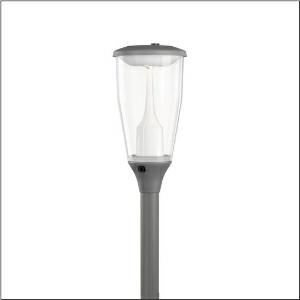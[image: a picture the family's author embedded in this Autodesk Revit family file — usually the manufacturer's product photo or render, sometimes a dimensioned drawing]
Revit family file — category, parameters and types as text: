
# Revit family: dl_11_iq___st1_2a_5xa5565ew14hp00022_746d
name_source: partatom
category: Lighting Fixtures
units: mm (PartAtom-declared; Revit-internal decimal feet)

## family parameters
Cut with Voids When Loaded = No
Host = Face
Light Source = No
Part Type = Normal
Room Calculation Point = No
Round Connector Dimension = Use Diameter
Shared = No

## types (1)
- --- (1 x LED, 4790 lm, 33.5 W, 3000K)
    Apparent Load = 34 VA
    CIE Flux Codes = 23 60 93 95 100
    Color Rendering = 70
    Color Temperature = 3000K
    Default Elevation = 1800 mm
    Description = DL 11 iQ, mast luminaire, Module 540 iQ-SR, primary light control with 3 zone facetted reflector, of plastic, silver coated, highly specular, structured, primary optical cover: cover, of PMMA, transparent, light distribution: ST1.2a, light emission: direct distribution, primary light characteristic: asymmetric, installation type: post-top, LED, High Power LED, rated luminous flux: 4.790lm, luminous efficacy: 143lm/W, light colour: 730, colour temperature: 3000K, control gear: iQ-Street Remote, D4i with power reduction, control: pre-setting: logarithmic dimming characteristic, Street-Remote, Auto-Match, Temp-Guard, Lumen-Switch, Night-Set, Smart-Wire, Light-Fading, Desk-Remote (wireless, voltage-free reading and setting of iQ features in the workshop via application-optimized NFC function/RFID function), optimised constant luminous flux control (CLO 2.0), mains connection: 220..240V, AC, 50/60Hz, connection cable pre-assembled, cable length: 5,5m, start of lifetime: 34W, end of service life: 36W, reduction: 15W, luminaire housing, upper part, of diecast aluminium, coated, Siteco® metallic grey (DB 702S), spigot size: 60mm (post-top), mounting height: 3..5m, post-top mast mounting element, of diecast aluminium, coated, Siteco® metallic grey (DB 702S), Module 540 iQ-SR, traffic white (RAL 9016), equipment: Power, Smart Interface above and design motion detector below, protection rating (complete): IP65, insulation class (complete): insulation class II (safety insulation), certification: CE, ENEC, ENEC+, VDE, impact resistance: IK07, packaging unit: 1 piece

Light Distribution: ST1.2a
    Height = 665 mm
    Lamp = 1 x LED
    Lamp Light Flux = 4790 lm
    Lamp Power = 33.5 W
    Lamp count = 1
    Length = 334 mm
    Luminous efficacy = 143 lm/W
    Manufacturer = Siteco
    ModVariant = No
    Model = 5XA5565EW14HP00022
    Number of Poles = 1
    OnlyDefault = Yes
    Power Factor = 1
    Product Name = DL 11 iQ | ST1.2a
    Product group = mast luminaire | pylon top
    ProductGroupID = 6100
    Protection Class = Protection class II
    Protection Degree = IP 65
    RLX_Detail_Level = 1
    RLX_Emergency_Light_Flux = 0 lm
    RLX_Emergency_Type = 0
    RLX_Emergency_Type_DB = No
    RlxData = <blob elided: 160857 chars, md5=4bd31208>
    Socket = socket
    Standby Power = 0 W
    System Light Flux = 4790 lm
    System Power = 34 W
    Type Comments = factory setting: luminous flux: 100 % | dim-lin: 254 | 695 mA
    Type Image = l_1337543.jpg
    URL = http://relux.com
    VarID = @adj_033930
    Voltage = 0 V
    Weight = 0.00 kg
    Width = 0 mm  [stored 0 ft]

note: [stored X ft] marks values corroborated as IEEE doubles in the binary element streams (Revit-internal decimal feet)

## geometry (parser evidence)
native form markers: Blend x4, Sweep x12
no freeform markers — native parametric forms only
